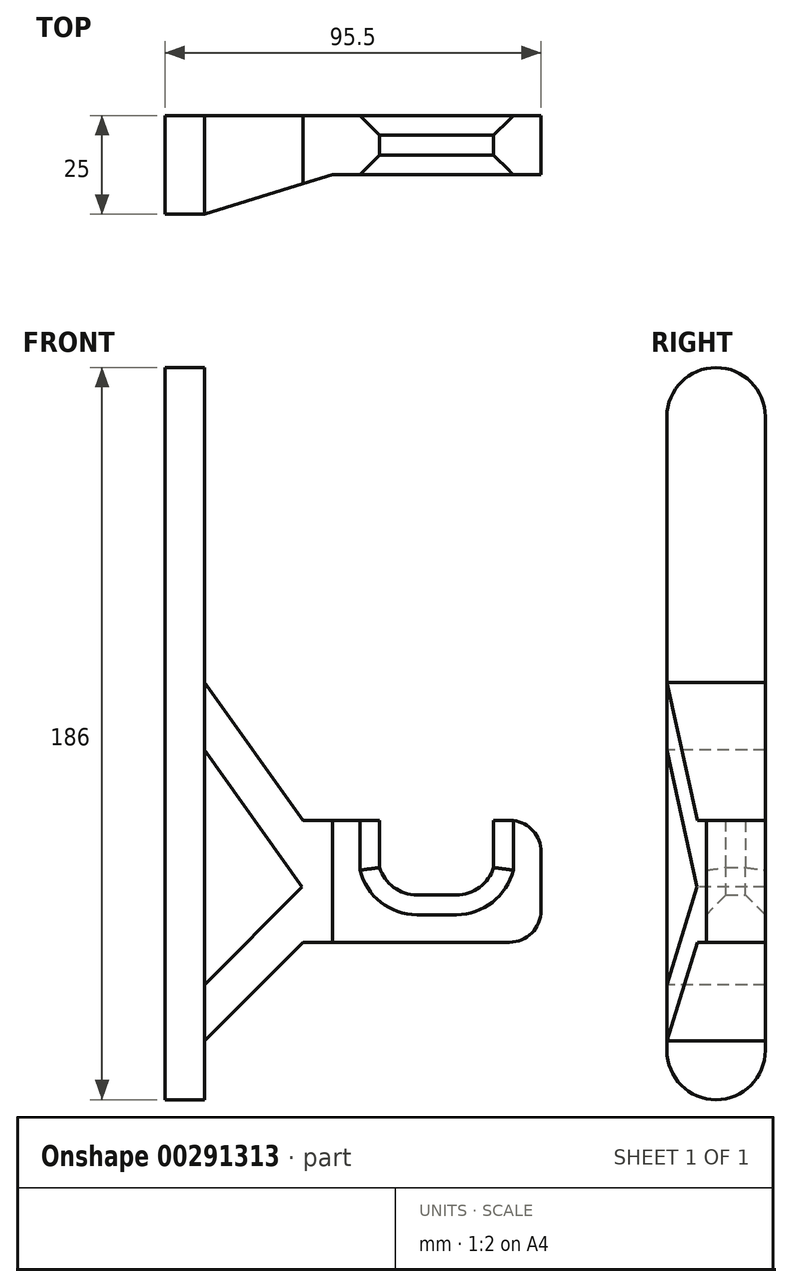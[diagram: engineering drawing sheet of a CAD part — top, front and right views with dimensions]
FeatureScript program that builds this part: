
annotation { "Feature Type Name" : "Feature", "Feature Type Description" : "" }
export const myFeature = defineFeature(function(context is Context, id is Id, definition is map)
    precondition{}
    {
        {
            var Q0;
            Q0=qCreatedBy(makeId("Front.planeOp"),FACE);
            var sketch = newSketch(context, id + "F0", { "sketchPlane" : qUnion([Q0])});
            skLineSegment(sketch, "E0", {"start": v(0, 0) * mm, "end": v(0, -12) * mm});
            skLineSegment(sketch, "E1", {"start": v(9.5, -19) * mm, "end": v(19.5, -19) * mm});
            skLineSegment(sketch, "E2", {"start": v(29, -12) * mm, "end": v(29, 0) * mm});
            skLineSegment(sketch, "E3", {"start": v(0, 0) * mm, "end": v(29, 0) * mm, "construction": true});
            skLineSegment(sketch, "E4", {"start": v(14.5, 0) * mm, "end": v(14.5, -19) * mm, "construction": true});
            skLineSegment(sketch, "E5.0", {"start": v(41, -31) * mm, "end": v(41, 0) * mm});
            skLineSegment(sketch, "E5.3", {"start": v(-44.5, -31) * mm, "end": v(41, -31) * mm});
            skLineSegment(sketch, "E6", {"start": v(29, 0) * mm, "end": v(41, 0) * mm});
            skLineSegment(sketch, "E7", {"start": v(-44.5, -31) * mm, "end": v(-44.5, -71) * mm});
            skLineSegment(sketch, "E8", {"start": v(-44.5, -71) * mm, "end": v(-54.5, -71) * mm});
            skLineSegment(sketch, "E9", {"start": v(-54.5, -71) * mm, "end": v(-54.5, 115) * mm});
            skLineSegment(sketch, "E10", {"start": v(-54.5, 115) * mm, "end": v(-44.5, 115) * mm});
            skLineSegment(sketch, "E11", {"start": v(-44.5, 115) * mm, "end": v(-44.5, 0) * mm});
            skLineSegment(sketch, "E12", {"start": v(-44.5, 0) * mm, "end": v(0, 0) * mm});
            skArc(sketch, "E13", {"start": v(0, -12) * mm, "mid": v(3.6, -17.06) * mm, "end": v(9.5, -19) * mm});
            skArc(sketch, "E14.MirrorCS", {"start": v(29, -12) * mm, "mid": v(25.4, -17.06) * mm, "end": v(19.5, -19) * mm});
            skSolve(sketch);
        }
        {
            var Q0;
            Q0=qSketchRegion(id+"F0",true);
            extrude(context, id + "F1", {"entities" : qUnion([Q0]), "depth" : 25 * mm});
        }
        {
            var Q0;
            Q0=makeQuery(id+"F1.opExtrude","SWEPT_FACE",FACE,{"disambiguationData":[OSD([sQuery(id+"F0.wireOp",EDGE,"E12")])]});
            var sketch = newSketch(context, id + "F2", { "sketchPlane" : qUnion([Q0])});
            skLineSegment(sketch, "E15", {"start": v(-44.5, -25) * mm, "end": v(-12, -15) * mm});
            skLineSegment(sketch, "E16", {"start": v(-12, -15) * mm, "end": v(48.06, -15) * mm});
            skLineSegment(sketch, "E17", {"start": v(48.06, -15) * mm, "end": v(48.06, -35.75) * mm});
            skLineSegment(sketch, "E18", {"start": v(48.06, -35.75) * mm, "end": v(-44.5, -35.75) * mm});
            skLineSegment(sketch, "E19", {"start": v(-44.5, -35.75) * mm, "end": v(-44.5, -25) * mm});
            skSolve(sketch);
        }
        {
            var Q0;
            Q0 = qSketchRegion(id + "F2", true);
            extrude(context, id + "F3", {"entities" : qUnion([Q0]), "operationType" : NewBodyOperationType.REMOVE, "endBound" : BoundingType.THROUGH_ALL, "oppositeDirection" : true, "depth" : 25 * mm});
        }
        {
            var Q0;
            Q0=makeQuery(id+"F3.boolean.opBoolean","INTERSECT",EDGE,{"derivedFrom":[makeQuery(id+"F1.opExtrude","SWEPT_FACE",FACE,{"disambiguationData":[OSD([sQuery(id+"F0.wireOp",EDGE,"E0")])]}),makeQuery(id+"F3.opExtrude","SWEPT_FACE",FACE,{"disambiguationData":[OSD([sQuery(id+"F2.wireOp",EDGE,"E16")])]})]});
            var Q1;
            Q1=makeQuery(id+"F3.boolean.opBoolean","INTERSECT",EDGE,{"derivedFrom":[makeQuery(id+"F1.opExtrude","SWEPT_FACE",FACE,{"disambiguationData":[OSD([sQuery(id+"F0.wireOp",EDGE,"E13")])]}),makeQuery(id+"F3.opExtrude","SWEPT_FACE",FACE,{"disambiguationData":[OSD([sQuery(id+"F2.wireOp",EDGE,"E16")])]})]});
            var Q2;
            Q2=makeQuery(id+"F3.boolean.opBoolean","INTERSECT",EDGE,{"derivedFrom":[makeQuery(id+"F1.opExtrude","SWEPT_FACE",FACE,{"disambiguationData":[OSD([sQuery(id+"F0.wireOp",EDGE,"E1")])]}),makeQuery(id+"F3.opExtrude","SWEPT_FACE",FACE,{"disambiguationData":[OSD([sQuery(id+"F2.wireOp",EDGE,"E16")])]})]});
            var Q3;
            Q3=makeQuery(id+"F3.boolean.opBoolean","INTERSECT",EDGE,{"derivedFrom":[makeQuery(id+"F1.opExtrude","SWEPT_FACE",FACE,{"disambiguationData":[OSD([sQuery(id+"F0.wireOp",EDGE,"E14.MirrorCS")])]}),makeQuery(id+"F3.opExtrude","SWEPT_FACE",FACE,{"disambiguationData":[OSD([sQuery(id+"F2.wireOp",EDGE,"E16")])]})]});
            var Q4;
            Q4=makeQuery(id+"F3.boolean.opBoolean","INTERSECT",EDGE,{"derivedFrom":[makeQuery(id+"F1.opExtrude","SWEPT_FACE",FACE,{"disambiguationData":[OSD([sQuery(id+"F0.wireOp",EDGE,"E2")])]}),makeQuery(id+"F3.opExtrude","SWEPT_FACE",FACE,{"disambiguationData":[OSD([sQuery(id+"F2.wireOp",EDGE,"E16")])]})]});
            chamfer(context, id + "F4", {"entities" : qUnion([Q0, Q1, Q2, Q3, Q4]), "chamferType" : ChamferType.TWO_OFFSETS, "width1" : 5 * mm, "oppositeDirection" : false, "width2" : 5 * mm, "tangentPropagation" : true});
        }
        {
            var Q0;
            Q0=makeQuery(id+"F1.opExtrude","CAP_EDGE",EDGE,{"disambiguationData":[OSD([sQuery(id+"F0.wireOp",EDGE,"E0")])],"isStart":true});
            var Q1;
            Q1=makeQuery(id+"F1.opExtrude","CAP_EDGE",EDGE,{"disambiguationData":[OSD([sQuery(id+"F0.wireOp",EDGE,"E13")])],"isStart":true});
            var Q2;
            Q2=makeQuery(id+"F1.opExtrude","CAP_EDGE",EDGE,{"disambiguationData":[OSD([sQuery(id+"F0.wireOp",EDGE,"E1")])],"isStart":true});
            var Q3;
            Q3=makeQuery(id+"F1.opExtrude","CAP_EDGE",EDGE,{"disambiguationData":[OSD([sQuery(id+"F0.wireOp",EDGE,"E14.MirrorCS")])],"isStart":true});
            var Q4;
            Q4=makeQuery(id+"F1.opExtrude","CAP_EDGE",EDGE,{"disambiguationData":[OSD([sQuery(id+"F0.wireOp",EDGE,"E2")])],"isStart":true});
            chamfer(context, id + "F5", {"entities" : qUnion([Q0, Q1, Q2, Q3, Q4]), "chamferType" : ChamferType.TWO_OFFSETS, "width1" : 5 * mm, "oppositeDirection" : false, "width2" : 5 * mm, "tangentPropagation" : true});
        }
        {
            var Q0;
            Q0=makeQuery(id+"F1.opExtrude","SWEPT_EDGE",EDGE,{"disambiguationData":[OSD([sQuery(id+"F0.wireOp",EDGE,"E5.0"),sQuery(id+"F0.wireOp",EDGE,"E5.3")])]});
            var Q1;
            Q1=makeQuery(id+"F1.opExtrude","SWEPT_EDGE",EDGE,{"disambiguationData":[OSD([sQuery(id+"F0.wireOp",EDGE,"E5.0"),sQuery(id+"F0.wireOp",EDGE,"E5.3")])]});
            var Q2;
            Q2=makeQuery(id+"F1.opExtrude","SWEPT_EDGE",EDGE,{"disambiguationData":[OSD([sQuery(id+"F0.wireOp",EDGE,"E5.0"),sQuery(id+"F0.wireOp",EDGE,"E6")])]});
            var Q3;
            Q3=makeQuery(id+"F1.opExtrude","SWEPT_EDGE",EDGE,{"disambiguationData":[OSD([sQuery(id+"F0.wireOp",EDGE,"E5.0"),sQuery(id+"F0.wireOp",EDGE,"E6")])]});
            fillet(context, id + "F6", {"entities" : qUnion([Q0, Q1, Q2, Q3]), "radius" : 8 * mm, "tangentPropagation" : true, "allowEdgeOverflow" : false});
        }
        {
            var Q0;
            Q0=makeQuery(id+"F1.opExtrude","CAP_EDGE",EDGE,{"disambiguationData":[OSD([sQuery(id+"F0.wireOp",EDGE,"E8")])],"isStart":false});
            var Q1;
            Q1=makeQuery(id+"F1.opExtrude","CAP_EDGE",EDGE,{"disambiguationData":[OSD([sQuery(id+"F0.wireOp",EDGE,"E8")])],"isStart":true});
            var Q2;
            Q2=makeQuery(id+"F1.opExtrude","CAP_EDGE",EDGE,{"disambiguationData":[OSD([sQuery(id+"F0.wireOp",EDGE,"E10")])],"isStart":false});
            var Q3;
            Q3=makeQuery(id+"F1.opExtrude","CAP_EDGE",EDGE,{"disambiguationData":[OSD([sQuery(id+"F0.wireOp",EDGE,"E10")])],"isStart":true});
            fillet(context, id + "F7", {"entities" : qUnion([Q0, Q1, Q2, Q3]), "radius" : 12.5 * mm, "tangentPropagation" : true, "allowEdgeOverflow" : false});
        }
        {
            var Q0;
            Q0=makeQuery(id+"F1.opExtrude","SWEPT_EDGE",EDGE,{"disambiguationData":[OSD([sQuery(id+"F0.wireOp",EDGE,"E11"),sQuery(id+"F0.wireOp",EDGE,"E12")])]});
            chamfer(context, id + "F8", {"entities" : qUnion([Q0]), "chamferType" : ChamferType.TWO_OFFSETS, "width1" : 35 * mm, "oppositeDirection" : false, "width2" : 25 * mm, "tangentPropagation" : true});
        }
        {
            var Q0;
            Q0=makeQuery(id+"F1.opExtrude","SWEPT_EDGE",EDGE,{"disambiguationData":[OSD([sQuery(id+"F0.wireOp",EDGE,"E5.3"),sQuery(id+"F0.wireOp",EDGE,"E7")])]});
            chamfer(context, id + "F9", {"entities" : qUnion([Q0]), "width" : 25 * mm, "tangentPropagation" : true});
        }
        {
            var Q0;
            Q0=makeQuery(id+"F1.opExtrude","CAP_FACE",FACE,{"disambiguationData":[OSD([sQuery(id+"F0.wireOp",EDGE,"E0"),sQuery(id+"F0.wireOp",EDGE,"UBh5Q6vy-bDk1-9Wx0-zEt8-RdoVWrF7CVSt"),sQuery(id+"F0.wireOp",EDGE,"E1"),sQuery(id+"F0.wireOp",EDGE,"GIhaa6fN-BBLZ-HFBX-1AUF-VRUvf6PevVMc"),sQuery(id+"F0.wireOp",EDGE,"E2"),sQuery(id+"F0.wireOp",EDGE,"E5.0"),sQuery(id+"F0.wireOp",EDGE,"E5.3"),sQuery(id+"F0.wireOp",EDGE,"E5.4"),sQuery(id+"F0.wireOp",EDGE,"E6"),sQuery(id+"F0.wireOp",EDGE,"E7"),sQuery(id+"F0.wireOp",EDGE,"E8"),sQuery(id+"F0.wireOp",EDGE,"E9"),sQuery(id+"F0.wireOp",EDGE,"E10"),sQuery(id+"F0.wireOp",EDGE,"E11"),sQuery(id+"F0.wireOp",EDGE,"E12")])],"isStart":false});
            var sketch = newSketch(context, id + "F10", { "sketchPlane" : qUnion([Q0])});
            skLineSegment(sketch, "E20", {"start": v(-44.5, 17.8) * mm, "end": v(-44.5, -41.86) * mm});
            skLineSegment(sketch, "E21", {"start": v(-44.5, -41.86) * mm, "end": v(-19.64, -17) * mm});
            skLineSegment(sketch, "E22", {"start": v(-19.64, -17) * mm, "end": v(-44.5, 17.8) * mm});
            skSolve(sketch);
        }
        {
            var Q0;
            Q0=qSketchRegion(id+"F10",true);
            extrude(context, id + "F11", {"entities" : qUnion([Q0]), "operationType" : NewBodyOperationType.REMOVE, "endBound" : BoundingType.THROUGH_ALL, "oppositeDirection" : true, "depth" : 25 * mm});
        }
    });
